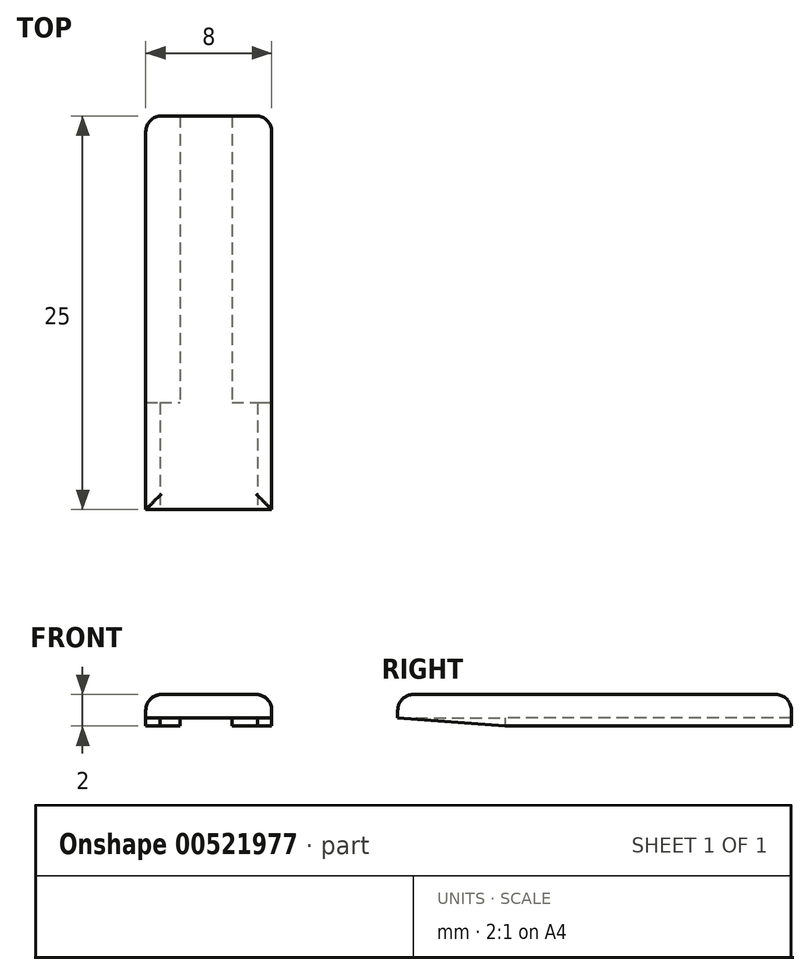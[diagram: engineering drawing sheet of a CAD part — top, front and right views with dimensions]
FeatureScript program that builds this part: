
annotation { "Feature Type Name" : "Feature", "Feature Type Description" : "" }
export const myFeature = defineFeature(function(context is Context, id is Id, definition is map)
    precondition{}
    {
        {
            var Q0;
            Q0=qCreatedBy(makeId("Top.planeOp"),FACE);
            var sketch = newSketch(context, id + "F0", { "sketchPlane" : qUnion([Q0])});
            skLineSegment(sketch, "E0.bottom", {"start": v(0, 0) * mm, "end": v(-8, 0) * mm});
            skLineSegment(sketch, "E0.top", {"start": v(0, 25) * mm, "end": v(-8, 25) * mm});
            skLineSegment(sketch, "E0.left", {"start": v(0, 0) * mm, "end": v(0, 25) * mm});
            skLineSegment(sketch, "E0.right", {"start": v(-8, 0) * mm, "end": v(-8, 25) * mm});
            skSolve(sketch);
        }
        {
            var Q0;
            Q0=makeQuery(id+"F0.imprint","IMPRINT",FACE,{"disambiguationData":[TD([[makeQuery(id+"F0.imprint","IMPRINT",EDGE,{"derivedFrom":sQuery(id+"F0.wireOp",EDGE,"E0.bottom")}),-1.0]])]});
            extrude(context, id + "F1", {"entities" : qUnion([Q0]), "depth" : 2 * mm, "offsetDistance" : 25 * mm});
        }
        {
            var Q0;
            Q0=makeQuery(id+"F1.opExtrude","CAP_FACE",FACE,{"disambiguationData":[OSD([sQuery(id+"F0.wireOp",EDGE,"E0.bottom"),sQuery(id+"F0.wireOp",EDGE,"E0.top"),sQuery(id+"F0.wireOp",EDGE,"E0.left"),sQuery(id+"F0.wireOp",EDGE,"E0.right")])],"isStart":true});
            var sketch = newSketch(context, id + "F2", { "sketchPlane" : qUnion([Q0])});
            skLineSegment(sketch, "E1.bottom", {"start": v(-5.83, -25) * mm, "end": v(-2.53, -25) * mm});
            skLineSegment(sketch, "E1.top", {"start": v(-5.83, -6.8) * mm, "end": v(-2.53, -6.8) * mm});
            skLineSegment(sketch, "E1.left", {"start": v(-5.83, -25) * mm, "end": v(-5.83, -6.8) * mm});
            skLineSegment(sketch, "E1.right", {"start": v(-2.53, -25) * mm, "end": v(-2.53, -6.8) * mm});
            skLineSegment(sketch, "E2", {"start": v(-4.18, -25) * mm, "end": v(-4.18, -25) * mm});
            skLineSegment(sketch, "E3.bottom", {"start": v(-7.1, 0) * mm, "end": v(-0.9, 0) * mm});
            skLineSegment(sketch, "E3.top", {"start": v(-7.1, -6.8) * mm, "end": v(-0.9, -6.8) * mm});
            skLineSegment(sketch, "E3.left", {"start": v(-7.1, 0) * mm, "end": v(-7.1, -6.8) * mm});
            skLineSegment(sketch, "E3.right", {"start": v(-0.9, 0) * mm, "end": v(-0.9, -6.8) * mm});
            skLineSegment(sketch, "E4", {"start": v(-7.1, -6.8) * mm, "end": v(-8, -25) * mm, "construction": true});
            skLineSegment(sketch, "E5", {"start": v(0, -25) * mm, "end": v(-0.9, -6.8) * mm, "construction": true});
            skSolve(sketch);
        }
        {
            var Q0;
            Q0=makeQuery(id+"F2.imprint","IMPRINT",FACE,{"disambiguationData":[TD([[makeQuery(id+"F2.imprint","IMPRINT",EDGE,{"derivedFrom":sQuery(id+"F2.wireOp",EDGE,"E3.bottom")}),1.0]])]});
            var Q1;
            Q1=makeQuery(id+"F2.imprint","IMPRINT",FACE,{"disambiguationData":[TD([[makeQuery(id+"F2.imprint","IMPRINT",EDGE,{"derivedFrom":sQuery(id+"F2.wireOp",EDGE,"E1.bottom")}),-1.0]])]});
            extrude(context, id + "F3", {"entities" : qUnion([Q0, Q1]), "operationType" : NewBodyOperationType.REMOVE, "oppositeDirection" : true, "depth" : 0.5 * mm, "offsetDistance" : 25 * mm});
        }
        {
            var Q0;
            Q0=makeQuery(id+"F1.opExtrude","SWEPT_FACE",FACE,{"disambiguationData":[OSD([sQuery(id+"F0.wireOp",EDGE,"E0.left")])]});
            var sketch = newSketch(context, id + "F4", { "sketchPlane" : qUnion([Q0])});
            skLineSegment(sketch, "E6", {"start": v(0, 0.5) * mm, "end": v(6.8, 0) * mm});
            skLineSegment(sketch, "E7", {"start": v(6.8, 0) * mm, "end": v(0, 0) * mm});
            skLineSegment(sketch, "E8", {"start": v(0, 0) * mm, "end": v(0, 0.5) * mm});
            skSolve(sketch);
        }
        {
            var Q0;
            Q0=makeQuery(id+"F4.imprint","IMPRINT",FACE,{"disambiguationData":[TD([[makeQuery(id+"F4.imprint","IMPRINT",EDGE,{"derivedFrom":sQuery(id+"F4.wireOp",EDGE,"E6")}),-1.0]])]});
            extrude(context, id + "F5", {"entities" : qUnion([Q0]), "operationType" : NewBodyOperationType.REMOVE, "endBound" : BoundingType.THROUGH_ALL, "oppositeDirection" : true, "depth" : 25 * mm, "offsetDistance" : 25 * mm});
        }
        {
            var Q0;
            Q0=makeQuery(id+"F1.opExtrude","SWEPT_EDGE",EDGE,{"disambiguationData":[OSD([sQuery(id+"F0.wireOp",EDGE,"E0.top"),sQuery(id+"F0.wireOp",EDGE,"E0.left")])]});
            var Q1;
            Q1=makeQuery(id+"F1.opExtrude","SWEPT_EDGE",EDGE,{"disambiguationData":[OSD([sQuery(id+"F0.wireOp",EDGE,"E0.top"),sQuery(id+"F0.wireOp",EDGE,"E0.right")])]});
            var Q2;
            Q2=makeQuery(id+"F1.opExtrude","CAP_EDGE",EDGE,{"disambiguationData":[OSD([sQuery(id+"F0.wireOp",EDGE,"E0.top")])],"isStart":false});
            var Q3;
            Q3=makeQuery(id+"F1.opExtrude","CAP_EDGE",EDGE,{"disambiguationData":[OSD([sQuery(id+"F0.wireOp",EDGE,"E0.left")])],"isStart":false});
            var Q4;
            Q4=makeQuery(id+"F1.opExtrude","CAP_EDGE",EDGE,{"disambiguationData":[OSD([sQuery(id+"F0.wireOp",EDGE,"E0.right")])],"isStart":false});
            var Q5;
            Q5=makeQuery(id+"F1.opExtrude","CAP_EDGE",EDGE,{"disambiguationData":[OSD([sQuery(id+"F0.wireOp",EDGE,"E0.bottom")])],"isStart":false});
            fillet(context, id + "F6", {"entities" : qUnion([Q0, Q1, Q2, Q3, Q4, Q5]), "radius" : 1 * mm, "tangentPropagation" : true, "allowEdgeOverflow" : false});
        }
    });
